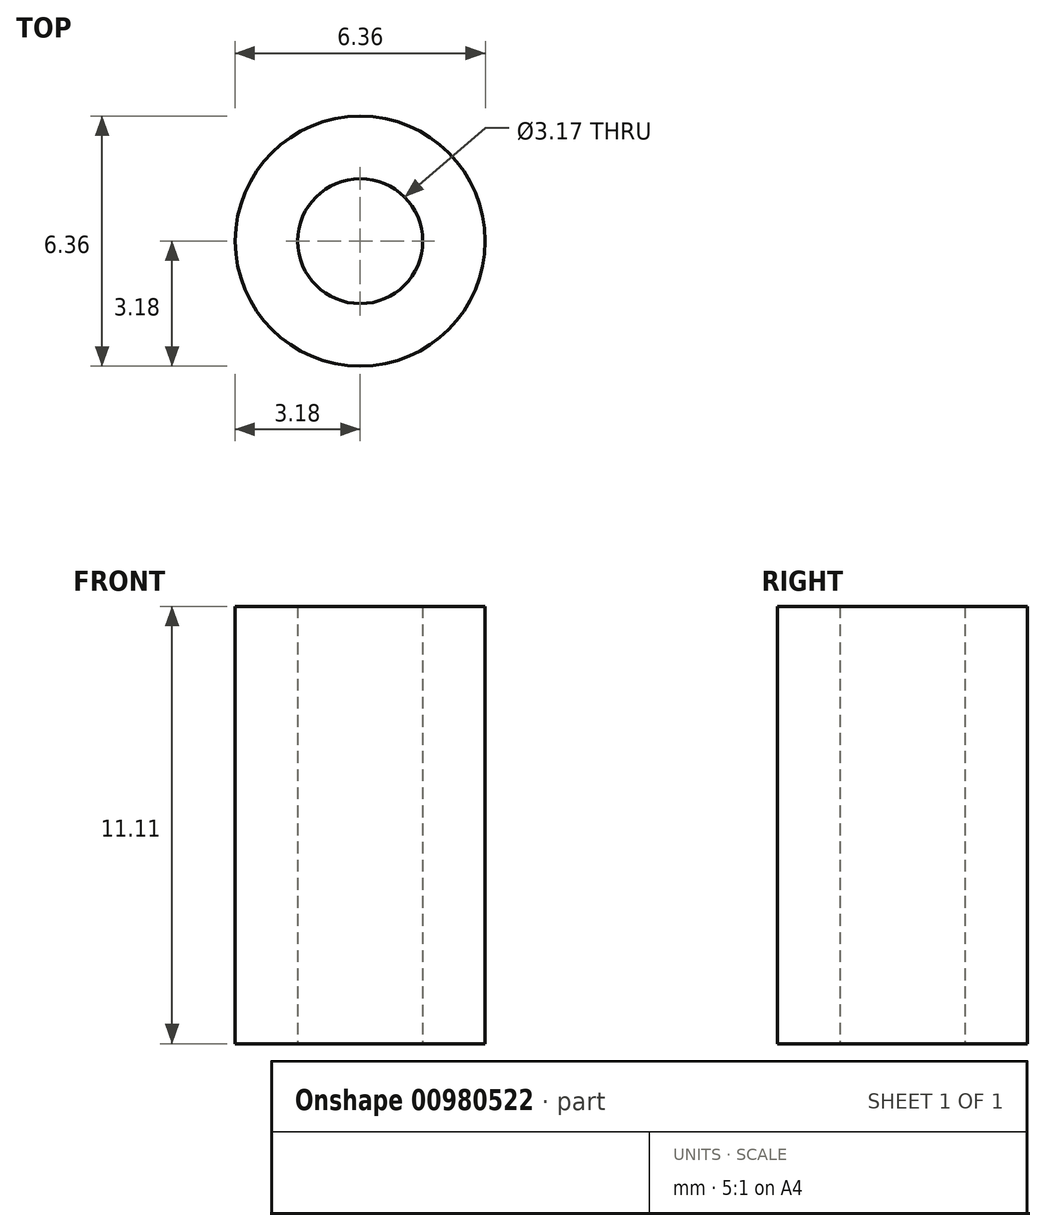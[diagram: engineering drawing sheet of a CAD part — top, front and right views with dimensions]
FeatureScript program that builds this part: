
annotation { "Feature Type Name" : "Feature", "Feature Type Description" : "" }
export const myFeature = defineFeature(function(context is Context, id is Id, definition is map)
    precondition{}
    {
        {
            var Q0;
            Q0=qCreatedBy(makeId("Top.planeOp"),FACE);
            var sketch = newSketch(context, id + "F0", { "sketchPlane" : qUnion([Q0])});
            skCircle(sketch, "E0", {"center": v(0, 0) * mm, "radius": 3.18 * mm});
            skCircle(sketch, "E1", {"center": v(0, 0) * mm, "radius": 1.59 * mm});
            skSolve(sketch);
        }
        {
            var Q0;
            Q0=makeQuery(id+"F0.imprint","IMPRINT",FACE,{"disambiguationData":[TD([[makeQuery(id+"F0.imprint","IMPRINT",EDGE,{"derivedFrom":sQuery(id+"F0.wireOp",EDGE,"E0")}),1.0]])]});
            extrude(context, id + "F1", {"entities" : qUnion([Q0]), "depth" : 11.1 * mm, "offsetDistance" : 25.4 * mm});
        }
    });
